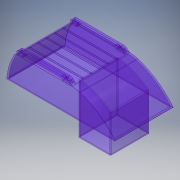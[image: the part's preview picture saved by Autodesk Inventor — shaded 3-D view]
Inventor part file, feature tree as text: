
AUTODESK INVENTOR PART (.ipt)
format: ipt  version: 2018 (Build 220112000, 112)  size: 378,368 bytes
history: native  units: in
note: dims shown in document units (in); Inventor stores cm internally (conversion verified against a paired STEP export)
features: extrude x8, sketch x8, shell x2, fillet x1, projected_geometry x1
ambient origin geometry x8: Origin, YZ Plane, XZ Plane, XY Plane, X Axis, Y Axis, Z Axis, Center Point
bodies: Solid1 (feature_tree)
feature tree (20):
  extrude  "Extrusion1"  Depth=0.4in
  shell  "Shell1"  Thickness=1.227in
  extrude  "Extrusion2"  Depth=0.125in
  extrude  "Extrusion3"  Depth=1.25in
  extrude  "Extrusion4"  Depth=2.75in TaperAngle=0.0deg
  extrude  "Extrusion5"  Depth=0.05in TaperAngle=0.0deg
  fillet  "Fillet1"  Radius=0.39in
  extrude  "Extrusion6"  Depth=0.18in
  extrude  "Extrusion7"  Depth=0.2in
  shell  "Shell2"  Thickness=0.05in
  extrude  "Extrusion8"  Depth=0.05in
  sketch  "Sketch1"  dims[d0=5.125in d1=0.4in d2=1.227in]
  sketch  "Sketch2"  dims[d3=2.825in d4=0.125in]
  sketch  "Sketch3"  dims[d5=0.025in d6=1.25in]
  sketch  "Sketch4"  dims[d7=0.015in d8=2.75in d9=0.0in]
  sketch  "Sketch5"  dims[d10=0.05in d11=0.05in d12=0.0in d14=0.39in]
  sketch  "Sketch6"  dims[d15=0.085in d16=0.18in]
  sketch  "Sketch7"  dims[d17=0.05in d18=0.2in d19=0.05in]
  projected_geometry  "Projected Loop1"
  sketch  "Sketch8"  dims[d20=2.75in d21=0.0in d22=0.215in d23=0.215in d24=0.01in d25=2.75in d26=0.0in d27=2.75in d28=0.01in d29=0.0099in d31=0.0325in d32=0.0325in d33=1.1275in d34=0.333in d35=0.065in d36=0.333in d37=0.065in d38=0.333in d39=0.065in d40=0.333in d41=0.065in d42=0.01in d43=0.0in d44=0.125in d45=0.65in d46=0.405in d47=0.405in d48=2.18in d49=0.05in d50=0.01in d51=0.0in d52=1.155in d53=0.0in d54=0.05in d55=0.01in d56=0.01in d57=0.0in d58=0.0in]
